# Revit family: BE_99403_de_DE
name_source: partatom
category: Leuchten
units: mm (PartAtom-declared; Revit-internal decimal feet)

## family parameters
Basisbauteil = Fläche
Beim Laden mit Abzugskörper schneiden = Ja
Bemaßung runder Anschluss = Durchmesser verwenden
Gemeinsam genutzt = Nein
Lichtquelle = Nein
Raumberechnungspunkt = Ja
Teiletyp = Normal

## types (4) — shared parameters
AC/DC = AC/DC
Aktualisierung = 2022-05-20T04:00:08
Anschlussleitung = 5.0 m ÖLFLEX 4 x 1²
BEGA_Dummy = Nein
BEGA_IES = Ja
BEGA_Intern = Ja
BEGA_Intern_Konstruktion = Ja
BEGA_Intern_an = Ja
BEGA_Intern_aus = Ja
Beschreibung = Aufsatzleuchte
Beschreibung_Sonderanfertigung = Hier können Sie Informationen zur Sonderanfertigung eintragen.
CE_Konformität = ja
ENEC = ja
Einstecktiefe = 50 mm
Energieeffizienzklasse = LED A++ - A
Farbwiedergabeindex = CRI > 80
Frequenz = 0/50-60 Hz
Gewicht = 7.25 kg
Hersteller = BEGA
Lampe = LED 32 W
Lastklassifizierung = Beleuchtung
Lebensdauerkriterien = L70B50 @ 25 °C = 200000 h
Logo = BEGA_Logo.png
M_W = Nein
Material_02 = BEGA_Oberfläche_Silber_matt
Material_03 = BEGA_Oberfläche_Weiss_matt
Material_06 = BEGA_Oberfläche_Edelstahl_gebürstet
Material_09 = BEGA_Glas_klar
Material_10 = BEGA_Glas_matt
Material_11 = BEGA_Glas_opal
Material_15 = BEGA_Leuchtmedium_matt
Material_17 = BEGA_Reflektor
Produktdatenblatt = https://cdn.bega.com
Scheinlast = 0 VA
Schutzart = IP 65
Schutzklasse = II
Sonderanfertigung = Nein
Spannung = 240 V
Typenbild = 99403.png
URL = https://www.bega.com
Umgebungstemperatur = 25 °C
Windangriffsfläche = 0.05 m²
zero-valued in all types: Vorgabe-Ansicht

## per-type parameters (varying)
| type | BEGA_IES1 | BEGA_IES2 | Bestellnummer | Farbtemperatur | LED_Modulbezeichnung | Lampenlichtstrom | Leuchtenlichtstrom | M_A | M_G | Modell |
| BEGA_99403_Grafit_K4 | Nein | Ja | 99403K4 | 4000 K | 8x LED-0299/840 | 5720 lm | 3998 lm | Nein | Ja | 99403K4 |
| BEGA_99403_Silber_K3 | Ja | Nein | 99403AK3 | 3000 K | 8x LED-0299/830 | 5640 lm | 3942 lm | Ja | Nein | 99403AK3 |
| BEGA_99403_Grafit_K3 | Ja | Nein | 99403K3 | 3000 K | 8x LED-0299/830 | 5640 lm | 3942 lm | Nein | Ja | 99403K3 |
| BEGA_99403_Silber_K4 | Nein | Ja | 99403AK4 | 4000 K | 8x LED-0299/840 | 5720 lm | 3998 lm | Ja | Nein | 99403AK4 |

## geometry (parser evidence)
native form markers: Sweep x2
no freeform markers — native parametric forms only
